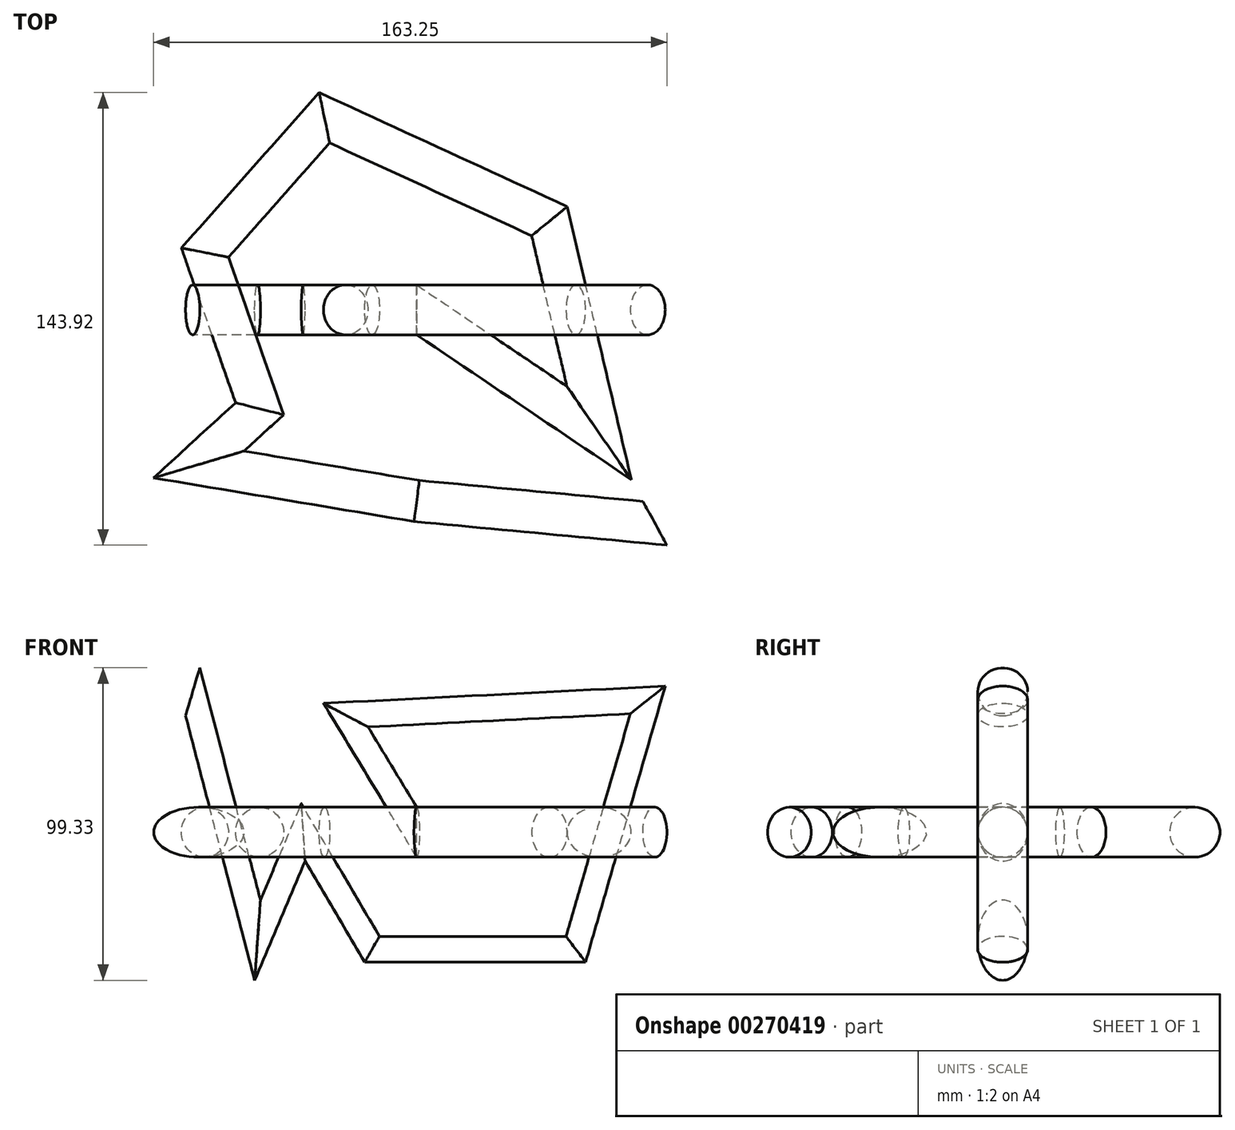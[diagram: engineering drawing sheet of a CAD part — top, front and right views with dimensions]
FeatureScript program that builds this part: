
annotation { "Feature Type Name" : "Feature", "Feature Type Description" : "" }
export const myFeature = defineFeature(function(context is Context, id is Id, definition is map)
    precondition{}
    {
        {
            var Q0;
            Q0=qCreatedBy(makeId("Top.planeOp"),FACE);
            var sketch = newSketch(context, id + "F0", { "sketchPlane" : qUnion([Q0])});
            skLineSegment(sketch, "E0", {"start": v(0, 0) * mm, "end": v(58.02, -39.16) * mm});
            skLineSegment(sketch, "E1", {"start": v(58.02, -39.16) * mm, "end": v(42.23, 28.2) * mm});
            skLineSegment(sketch, "E2", {"start": v(42.23, 28.2) * mm, "end": v(-29.33, 61.08) * mm});
            skLineSegment(sketch, "E3", {"start": v(-29.33, 61.08) * mm, "end": v(-67.37, 18.21) * mm});
            skLineSegment(sketch, "E4", {"start": v(-67.37, 18.21) * mm, "end": v(-49.96, -31.43) * mm});
            skLineSegment(sketch, "E5", {"start": v(-49.96, -31.43) * mm, "end": v(-69.3, -49.16) * mm});
            skLineSegment(sketch, "E6", {"start": v(-69.3, -49.16) * mm, "end": v(0, -60.76) * mm});
            skLineSegment(sketch, "E7", {"start": v(0, -60.76) * mm, "end": v(75.75, -67.85) * mm});
            skSolve(sketch);
        }
        {
            var Q0;
            Q0=qCreatedBy(makeId("Front.planeOp"),FACE);
            var sketch = newSketch(context, id + "F1", { "sketchPlane" : qUnion([Q0])});
            skLineSegment(sketch, "E8", {"start": v(0, 0) * mm, "end": v(-22.56, 37.23) * mm});
            skLineSegment(sketch, "E9", {"start": v(-22.56, 37.23) * mm, "end": v(73.5, 42.06) * mm});
            skLineSegment(sketch, "E10", {"start": v(73.5, 42.06) * mm, "end": v(50.6, -37.23) * mm});
            skLineSegment(sketch, "E11", {"start": v(50.6, -37.23) * mm, "end": v(-14.18, -37.23) * mm});
            skLineSegment(sketch, "E12", {"start": v(-14.18, -37.23) * mm, "end": v(-36.1, 0) * mm});
            skLineSegment(sketch, "E13", {"start": v(-36.1, 0) * mm, "end": v(-50.6, -34.33) * mm});
            skLineSegment(sketch, "E14", {"start": v(-50.6, -34.33) * mm, "end": v(-71.24, 44.64) * mm});
            skSolve(sketch);
        }
        {
            var Q0;
            Q0=qCreatedBy(makeId("Right.planeOp"),FACE);
            var sketch = newSketch(context, id + "F2", { "sketchPlane" : qUnion([Q0])});
            skCircle(sketch, "E15", {"center": v(0, 0) * mm, "radius": 7.94 * mm});
            skSolve(sketch);
        }
        {
            var Q0;
            Q0=makeQuery(id+"F2.imprint","IMPRINT",FACE,{"disambiguationData":[TD([[makeQuery(id+"F2.imprint","IMPRINT",EDGE,{"derivedFrom":sQuery(id+"F2.wireOp",EDGE,"E15")}),1.0]])]});
            var Q1;
            Q1=sQuery(id+"F0.wireOp",EDGE,"E0");
            var Q2;
            Q2=sQuery(id+"F0.wireOp",EDGE,"E1");
            var Q3;
            Q3=sQuery(id+"F0.wireOp",EDGE,"E2");
            var Q4;
            Q4=sQuery(id+"F0.wireOp",EDGE,"E3");
            var Q5;
            Q5=sQuery(id+"F0.wireOp",EDGE,"E4");
            var Q6;
            Q6=sQuery(id+"F0.wireOp",EDGE,"E5");
            var Q7;
            Q7=sQuery(id+"F0.wireOp",EDGE,"E6");
            var Q8;
            Q8=sQuery(id+"F0.wireOp",EDGE,"E7");
            sweep(context, id + "F3", {"profiles" : qUnion([Q0]), "path" : qUnion([Q1, Q2, Q3, Q4, Q5, Q6, Q7, Q8])});
        }
        {
            var Q0;
            Q0=makeQuery(id+"F2.imprint","IMPRINT",FACE,{"disambiguationData":[TD([[makeQuery(id+"F2.imprint","IMPRINT",EDGE,{"derivedFrom":sQuery(id+"F2.wireOp",EDGE,"E15")}),1.0]])]});
            var Q1;
            Q1=sQuery(id+"F1.wireOp",EDGE,"E8");
            var Q2;
            Q2=sQuery(id+"F1.wireOp",EDGE,"E9");
            var Q3;
            Q3=sQuery(id+"F1.wireOp",EDGE,"E10");
            var Q4;
            Q4=sQuery(id+"F1.wireOp",EDGE,"E11");
            var Q5;
            Q5=sQuery(id+"F1.wireOp",EDGE,"E12");
            var Q6;
            Q6=sQuery(id+"F1.wireOp",EDGE,"E13");
            var Q7;
            Q7=sQuery(id+"F1.wireOp",EDGE,"E14");
            sweep(context, id + "F4", {"profiles" : qUnion([Q0]), "path" : qUnion([Q1, Q2, Q3, Q4, Q5, Q6, Q7])});
        }
    });
